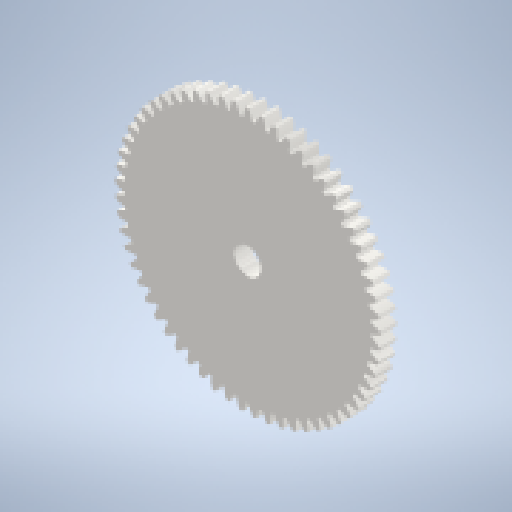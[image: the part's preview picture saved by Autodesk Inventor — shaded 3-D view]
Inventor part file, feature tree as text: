
AUTODESK INVENTOR PART (.ipt)
format: ipt  version: 2024 (Build 280153000, 153)  size: 406,528 bytes
history: native  units: mm (DEFAULTED — no unit token found)
features: plane x3, other x3, extrude x2, sketch x2
ambient origin geometry x8: Origin, YZ Plane, XZ Plane, XY Plane, X Axis, Y Axis, Z Axis, Center Point
bodies: Solid1 (feature_tree)
feature tree (10):
  extrude  "Extrusion1"  Depth=3.175mm TaperAngle=0.0deg
  plane  "Work Plane1"
  plane  "Work Plane2"
  plane  "Work Plane3"
  other  "Spur Gear"
  extrude  "Extrusion2"  Depth=76.2mm TaperAngle=0.0deg
  sketch  "Sketch1"  dims[d0=50.0761mm d1=3.175mm d2=0.0mm]
  other  "Srf1"
  sketch  "Sketch3"  dims[d3=48.41875mm d4=76.2mm d5=0.0mm d6=0.0mm d7=0.515015mm d9=0.0mm d14=0.0mm d15=32.1818mm d16=0.0mm d17=0.0mm d18=0.0mm d19=32.1818mm d20=5.0mm d21=25.4mm d22=0.0mm]
  other  "Pitch Diameter"
